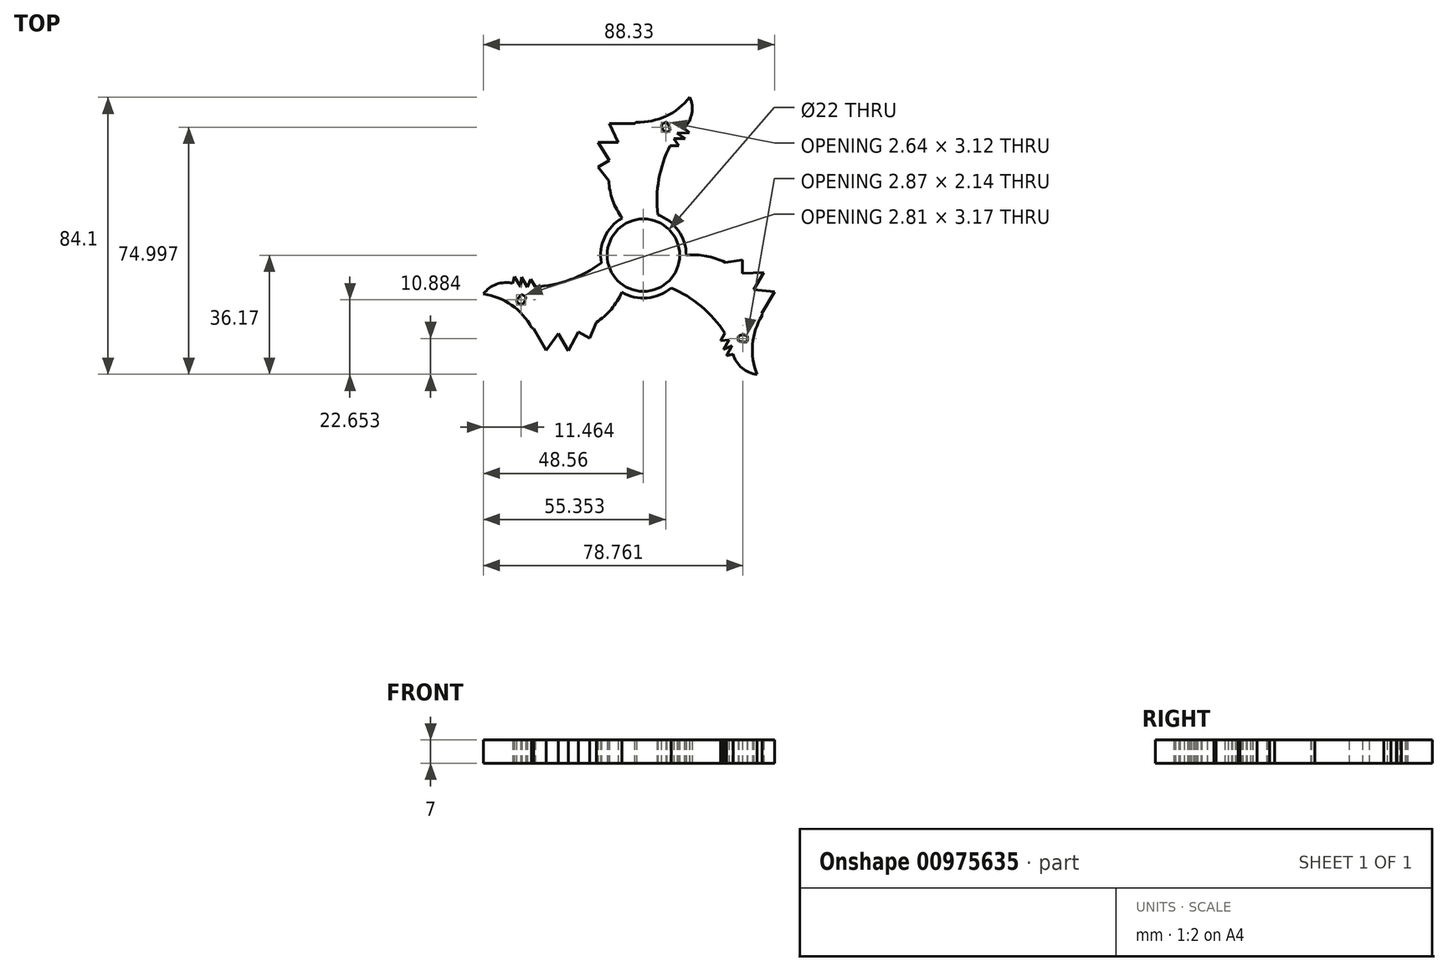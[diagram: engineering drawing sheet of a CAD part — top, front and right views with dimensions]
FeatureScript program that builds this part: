
annotation { "Feature Type Name" : "Feature", "Feature Type Description" : "" }
export const myFeature = defineFeature(function(context is Context, id is Id, definition is map)
    precondition{}
    {
        {
            var Q0;
            Q0=qCreatedBy(makeId("Top.planeOp"),FACE);
            var sketch = newSketch(context, id + "F0", { "sketchPlane" : qUnion([Q0])});
            skCircle(sketch, "E0", {"center": v(0, 0) * mm, "radius": 11 * mm});
            skCircle(sketch, "E1.0", {"center": v(0, 0) * mm, "radius": 13 * mm});
            skArc(sketch, "E2", {"start": v(-2.12, 40.39) * mm, "mid": v(-10.32, 26.74) * mm, "end": v(-6.45, 11.29) * mm});
            skArc(sketch, "E3", {"start": v(10.3, 37.05) * mm, "mid": v(5.14, 25.17) * mm, "end": v(4.36, 12.25) * mm});
            skLineSegment(sketch, "E4", {"start": v(-10.52, 22.62) * mm, "end": v(-13.72, 26.74) * mm});
            skPoint(sketch, "E4.endSnap0", {"position": v(-10.32, 26.74) * mm});
            skLineSegment(sketch, "E5", {"start": v(-13.72, 26.74) * mm, "end": v(-10.32, 28.79) * mm});
            skLineSegment(sketch, "E6", {"start": v(-10.32, 28.79) * mm, "end": v(-13.72, 34.2) * mm});
            skLineSegment(sketch, "E7", {"start": v(-13.72, 34.2) * mm, "end": v(-7.69, 34.2) * mm});
            skLineSegment(sketch, "E8", {"start": v(-7.69, 34.2) * mm, "end": v(-10.32, 39.97) * mm});
            skLineSegment(sketch, "E9", {"start": v(-10.32, 39.97) * mm, "end": v(-2.67, 39.97) * mm});
            skArc(sketch, "E10", {"start": v(-2.12, 40.39) * mm, "mid": v(6.9, 42.22) * mm, "end": v(14.08, 47.93) * mm});
            skArc(sketch, "E11", {"start": v(10.3, 37.05) * mm, "mid": v(14.34, 41.74) * mm, "end": v(14.08, 47.93) * mm});
            skArc(sketch, "E12", {"start": v(10.3, 40.39) * mm, "mid": v(6.12, 40.04) * mm, "end": v(3.2, 37.05) * mm});
            skArc(sketch, "E13", {"start": v(3.2, 37.05) * mm, "mid": v(7.33, 37.47) * mm, "end": v(10.3, 40.39) * mm});
            skArc(sketch, "E14", {"start": v(5.47, 39.69) * mm, "mid": v(5.85, 38.3) * mm, "end": v(6.83, 37.26) * mm});
            skArc(sketch, "E15", {"start": v(8.11, 37.91) * mm, "mid": v(7.75, 39.22) * mm, "end": v(7.05, 40.39) * mm});
            skLineSegment(sketch, "E16", {"start": v(8.1, 33.26) * mm, "end": v(10.79, 33.26) * mm});
            skLineSegment(sketch, "E17", {"start": v(10.79, 33.26) * mm, "end": v(9.25, 35.36) * mm});
            skLineSegment(sketch, "E18", {"start": v(9.25, 35.36) * mm, "end": v(12.68, 35.36) * mm});
            skLineSegment(sketch, "E19", {"start": v(12.68, 35.36) * mm, "end": v(10.3, 37.05) * mm});
            skLineSegment(sketch, "E20", {"start": v(10.3, 37.05) * mm, "end": v(13.87, 37.16) * mm});
            skLineSegment(sketch, "E21", {"start": v(13.87, 37.16) * mm, "end": v(12.38, 38.6) * mm});
            skArc(sketch, "E22.1.0", {"start": v(-33.92, -22.03) * mm, "mid": v(-18, -22.3) * mm, "end": v(-6.55, -11.23) * mm});
            skArc(sketch, "E22.1.1", {"start": v(-37.23, -9.6) * mm, "mid": v(-24.37, -8.14) * mm, "end": v(-12.79, -2.35) * mm});
            skArc(sketch, "E22.1.2", {"start": v(-37.23, -9.6) * mm, "mid": v(-43.32, -8.46) * mm, "end": v(-48.56, -11.77) * mm});
            skArc(sketch, "E22.1.3", {"start": v(-33.92, -22.03) * mm, "mid": v(-40, -15.14) * mm, "end": v(-48.56, -11.77) * mm});
            skArc(sketch, "E22.1.4", {"start": v(-33.68, -15.76) * mm, "mid": v(-36.12, -12.39) * mm, "end": v(-40.13, -11.28) * mm});
            skArc(sketch, "E22.1.5", {"start": v(-40.13, -11.28) * mm, "mid": v(-37.74, -14.72) * mm, "end": v(-33.68, -15.76) * mm});
            skArc(sketch, "E22.1.6", {"start": v(-36.89, -11.93) * mm, "mid": v(-37.84, -12.9) * mm, "end": v(-38.5, -14.09) * mm});
            skArc(sketch, "E22.1.7", {"start": v(-37.1, -15.1) * mm, "mid": v(-36.1, -14.09) * mm, "end": v(-35.69, -12.71) * mm});
            skLineSegment(sketch, "E22.1.8", {"start": v(-39.11, -6.57) * mm, "end": v(-39.61, -8.58) * mm});
            skLineSegment(sketch, "E22.1.9", {"start": v(-37.23, -9.6) * mm, "end": v(-39.11, -6.57) * mm});
            skLineSegment(sketch, "E22.1.10", {"start": v(-35.25, -9.67) * mm, "end": v(-36.96, -6.7) * mm});
            skLineSegment(sketch, "E22.1.11", {"start": v(-36.96, -6.7) * mm, "end": v(-37.23, -9.6) * mm});
            skLineSegment(sketch, "E22.1.12", {"start": v(-34.2, -7.29) * mm, "end": v(-35.25, -9.67) * mm});
            skLineSegment(sketch, "E22.1.13", {"start": v(-32.86, -9.61) * mm, "end": v(-34.2, -7.29) * mm});
            skLineSegment(sketch, "E22.1.14", {"start": v(-14.33, -20.42) * mm, "end": v(-16.3, -25.25) * mm});
            skLineSegment(sketch, "E22.1.15", {"start": v(-16.3, -25.25) * mm, "end": v(-19.77, -23.33) * mm});
            skLineSegment(sketch, "E22.1.16", {"start": v(-19.77, -23.33) * mm, "end": v(-22.76, -28.98) * mm});
            skLineSegment(sketch, "E22.1.17", {"start": v(-25.77, -23.76) * mm, "end": v(-29.45, -28.92) * mm});
            skLineSegment(sketch, "E22.1.18", {"start": v(-29.45, -28.92) * mm, "end": v(-33.28, -22.3) * mm});
            skLineSegment(sketch, "E22.1.19", {"start": v(-22.76, -28.98) * mm, "end": v(-25.77, -23.76) * mm});
            skArc(sketch, "E22.2.0", {"start": v(36.04, -18.36) * mm, "mid": v(28.32, -4.43) * mm, "end": v(13, -0.06) * mm});
            skArc(sketch, "E22.2.1", {"start": v(26.93, -27.44) * mm, "mid": v(19.23, -17.04) * mm, "end": v(8.43, -9.9) * mm});
            skArc(sketch, "E22.2.2", {"start": v(26.93, -27.44) * mm, "mid": v(28.98, -33.29) * mm, "end": v(34.47, -36.17) * mm});
            skArc(sketch, "E22.2.3", {"start": v(36.04, -18.36) * mm, "mid": v(33.11, -27.08) * mm, "end": v(34.47, -36.17) * mm});
            skArc(sketch, "E22.2.4", {"start": v(30.48, -21.3) * mm, "mid": v(28.79, -25.09) * mm, "end": v(29.83, -29.11) * mm});
            skArc(sketch, "E22.2.5", {"start": v(29.83, -29.11) * mm, "mid": v(31.62, -25.32) * mm, "end": v(30.48, -21.3) * mm});
            skArc(sketch, "E22.2.6", {"start": v(28.78, -25.98) * mm, "mid": v(30.1, -26.32) * mm, "end": v(31.45, -26.3) * mm});
            skArc(sketch, "E22.2.7", {"start": v(31.63, -24.58) * mm, "mid": v(30.25, -24.21) * mm, "end": v(28.85, -24.55) * mm});
            skLineSegment(sketch, "E22.2.8", {"start": v(25.25, -30.59) * mm, "end": v(27.23, -30.01) * mm});
            skLineSegment(sketch, "E22.2.9", {"start": v(26.93, -27.44) * mm, "end": v(25.25, -30.59) * mm});
            skLineSegment(sketch, "E22.2.10", {"start": v(26, -25.69) * mm, "end": v(24.28, -28.66) * mm});
            skLineSegment(sketch, "E22.2.11", {"start": v(24.28, -28.66) * mm, "end": v(26.93, -27.44) * mm});
            skLineSegment(sketch, "E22.2.12", {"start": v(23.41, -25.97) * mm, "end": v(26, -25.69) * mm});
            skLineSegment(sketch, "E22.2.13", {"start": v(24.75, -23.65) * mm, "end": v(23.41, -25.97) * mm});
            skLineSegment(sketch, "E22.2.14", {"start": v(24.85, -2.2) * mm, "end": v(30.01, -1.5) * mm});
            skLineSegment(sketch, "E22.2.15", {"start": v(30.01, -1.5) * mm, "end": v(30.1, -5.46) * mm});
            skLineSegment(sketch, "E22.2.16", {"start": v(30.1, -5.46) * mm, "end": v(36.48, -5.22) * mm});
            skLineSegment(sketch, "E22.2.17", {"start": v(33.46, -10.44) * mm, "end": v(39.77, -11.04) * mm});
            skLineSegment(sketch, "E22.2.18", {"start": v(39.77, -11.04) * mm, "end": v(35.95, -17.67) * mm});
            skLineSegment(sketch, "E22.2.19", {"start": v(36.48, -5.22) * mm, "end": v(33.46, -10.44) * mm});
            skSolve(sketch);
        }
        {
            var Q0;
            {var subQ16=sQuery(id+"F0.wireOp",EDGE,"E10");Q0=makeQuery(id+"F0.imprint","IMPRINT",FACE,{"disambiguationData":[TD([[makeQuery(id+"F0.imprint","IMPRINT",EDGE,{"derivedFrom":subQ16}),-1.0]])]});}
            var Q1;
            {var subQ0=sQuery(id+"F0.wireOp",EDGE,"E8");Q1=makeQuery(id+"F0.imprint","IMPRINT",FACE,{"disambiguationData":[TD([[makeQuery(id+"F0.imprint","IMPRINT",EDGE,{"derivedFrom":subQ0}),-1.0]])]});}
            var Q2;
            {var subQ0=sQuery(id+"F0.wireOp",EDGE,"E4");Q2=makeQuery(id+"F0.imprint","IMPRINT",FACE,{"disambiguationData":[TD([[makeQuery(id+"F0.imprint","IMPRINT",EDGE,{"derivedFrom":subQ0}),-1.0]])]});}
            var Q3;
            {var subQ0=sQuery(id+"F0.wireOp",EDGE,"E20");Q3=makeQuery(id+"F0.imprint","IMPRINT",FACE,{"disambiguationData":[TD([[makeQuery(id+"F0.imprint","IMPRINT",EDGE,{"derivedFrom":subQ0}),1.0]])]});}
            var Q4;
            {var subQ2=sQuery(id+"F0.wireOp",EDGE,"E18");Q4=makeQuery(id+"F0.imprint","IMPRINT",FACE,{"disambiguationData":[TD([[makeQuery(id+"F0.imprint","IMPRINT",EDGE,{"derivedFrom":subQ2}),1.0]])]});}
            var Q5;
            {var subQ0=sQuery(id+"F0.wireOp",EDGE,"E16");Q5=makeQuery(id+"F0.imprint","IMPRINT",FACE,{"disambiguationData":[TD([[makeQuery(id+"F0.imprint","IMPRINT",EDGE,{"derivedFrom":subQ0}),1.0]])]});}
            var Q6;
            {var subQ0=sQuery(id+"F0.wireOp",EDGE,"E22.2.3");Q6=makeQuery(id+"F0.imprint","IMPRINT",FACE,{"disambiguationData":[TD([[makeQuery(id+"F0.imprint","IMPRINT",EDGE,{"derivedFrom":subQ0}),-1.0]])]});}
            var Q7;
            {var subQ0=sQuery(id+"F0.wireOp",EDGE,"E22.2.17");Q7=makeQuery(id+"F0.imprint","IMPRINT",FACE,{"disambiguationData":[TD([[makeQuery(id+"F0.imprint","IMPRINT",EDGE,{"derivedFrom":subQ0}),-1.0]])]});}
            var Q8;
            {var subQ0=sQuery(id+"F0.wireOp",EDGE,"E22.2.14");Q8=makeQuery(id+"F0.imprint","IMPRINT",FACE,{"disambiguationData":[TD([[makeQuery(id+"F0.imprint","IMPRINT",EDGE,{"derivedFrom":subQ0}),-1.0]])]});}
            var Q9;
            {var subQ0=sQuery(id+"F0.wireOp",EDGE,"E22.2.12");Q9=makeQuery(id+"F0.imprint","IMPRINT",FACE,{"disambiguationData":[TD([[makeQuery(id+"F0.imprint","IMPRINT",EDGE,{"derivedFrom":subQ0}),1.0]])]});}
            var Q10;
            {var subQ2=sQuery(id+"F0.wireOp",EDGE,"E22.2.10");Q10=makeQuery(id+"F0.imprint","IMPRINT",FACE,{"disambiguationData":[TD([[makeQuery(id+"F0.imprint","IMPRINT",EDGE,{"derivedFrom":subQ2}),1.0]])]});}
            var Q11;
            {var subQ2=sQuery(id+"F0.wireOp",EDGE,"E22.2.8");Q11=makeQuery(id+"F0.imprint","IMPRINT",FACE,{"disambiguationData":[TD([[makeQuery(id+"F0.imprint","IMPRINT",EDGE,{"derivedFrom":subQ2}),1.0]])]});}
            var Q12;
            {var subQ3=sQuery(id+"F0.wireOp",EDGE,"E22.2.7");Q12=makeQuery(id+"F0.imprint","IMPRINT",FACE,{"disambiguationData":[TD([[makeQuery(id+"F0.imprint","IMPRINT",EDGE,{"derivedFrom":subQ3}),-1.0]])]});}
            var Q13;
            {var subQ3=sQuery(id+"F0.wireOp",EDGE,"E22.2.6");Q13=makeQuery(id+"F0.imprint","IMPRINT",FACE,{"disambiguationData":[TD([[makeQuery(id+"F0.imprint","IMPRINT",EDGE,{"derivedFrom":subQ3}),-1.0]])]});}
            var Q14;
            {var subQ3=sQuery(id+"F0.wireOp",EDGE,"E15");Q14=makeQuery(id+"F0.imprint","IMPRINT",FACE,{"disambiguationData":[TD([[makeQuery(id+"F0.imprint","IMPRINT",EDGE,{"derivedFrom":subQ3}),-1.0]])]});}
            var Q15;
            {var subQ3=sQuery(id+"F0.wireOp",EDGE,"E14");Q15=makeQuery(id+"F0.imprint","IMPRINT",FACE,{"disambiguationData":[TD([[makeQuery(id+"F0.imprint","IMPRINT",EDGE,{"derivedFrom":subQ3}),-1.0]])]});}
            var Q16;
            {var subQ0=sQuery(id+"F0.wireOp",EDGE,"E22.1.12");Q16=makeQuery(id+"F0.imprint","IMPRINT",FACE,{"disambiguationData":[TD([[makeQuery(id+"F0.imprint","IMPRINT",EDGE,{"derivedFrom":subQ0}),1.0]])]});}
            var Q17;
            {var subQ2=sQuery(id+"F0.wireOp",EDGE,"E22.1.10");Q17=makeQuery(id+"F0.imprint","IMPRINT",FACE,{"disambiguationData":[TD([[makeQuery(id+"F0.imprint","IMPRINT",EDGE,{"derivedFrom":subQ2}),1.0]])]});}
            var Q18;
            {var subQ2=sQuery(id+"F0.wireOp",EDGE,"E22.1.8");Q18=makeQuery(id+"F0.imprint","IMPRINT",FACE,{"disambiguationData":[TD([[makeQuery(id+"F0.imprint","IMPRINT",EDGE,{"derivedFrom":subQ2}),1.0]])]});}
            var Q19;
            {var subQ0=sQuery(id+"F0.wireOp",EDGE,"E22.1.17");Q19=makeQuery(id+"F0.imprint","IMPRINT",FACE,{"disambiguationData":[TD([[makeQuery(id+"F0.imprint","IMPRINT",EDGE,{"derivedFrom":subQ0}),-1.0]])]});}
            var Q20;
            {var subQ0=sQuery(id+"F0.wireOp",EDGE,"E22.1.14");Q20=makeQuery(id+"F0.imprint","IMPRINT",FACE,{"disambiguationData":[TD([[makeQuery(id+"F0.imprint","IMPRINT",EDGE,{"derivedFrom":subQ0}),-1.0]])]});}
            var Q21;
            {var subQ3=sQuery(id+"F0.wireOp",EDGE,"E22.1.7");Q21=makeQuery(id+"F0.imprint","IMPRINT",FACE,{"disambiguationData":[TD([[makeQuery(id+"F0.imprint","IMPRINT",EDGE,{"derivedFrom":subQ3}),-1.0]])]});}
            var Q22;
            {var subQ0=sQuery(id+"F0.wireOp",EDGE,"E22.1.3");Q22=makeQuery(id+"F0.imprint","IMPRINT",FACE,{"disambiguationData":[TD([[makeQuery(id+"F0.imprint","IMPRINT",EDGE,{"derivedFrom":subQ0}),-1.0]])]});}
            var Q23;
            {var subQ3=sQuery(id+"F0.wireOp",EDGE,"E22.1.6");Q23=makeQuery(id+"F0.imprint","IMPRINT",FACE,{"disambiguationData":[TD([[makeQuery(id+"F0.imprint","IMPRINT",EDGE,{"derivedFrom":subQ3}),-1.0]])]});}
            var Q24;
            Q24=makeQuery(id+"F0.imprint","IMPRINT",FACE,{"disambiguationData":[TD([[makeQuery(id+"F0.imprint","IMPRINT",EDGE,{"derivedFrom":sQuery(id+"F0.wireOp",EDGE,"E0")}),-1.0]])]});
            extrude(context, id + "F1", {"entities" : qUnion([Q0, Q1, Q2, Q3, Q4, Q5, Q6, Q7, Q8, Q9, Q10, Q11, Q12, Q13, Q14, Q15, Q16, Q17, Q18, Q19, Q20, Q21, Q22, Q23, Q24]), "depth" : 7 * mm, "offsetDistance" : 25 * mm});
        }
    });
